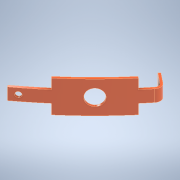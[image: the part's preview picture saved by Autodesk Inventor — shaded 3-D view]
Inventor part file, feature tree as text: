
AUTODESK INVENTOR PART (.ipt)
format: ipt  version: 2021 (Build 250183000, 183)  size: 205,824 bytes
history: native  units: in
note: dims shown in document units (in); Inventor stores cm internally (conversion verified against a paired STEP export)
features: other x5, sketch x4, extrude x1, plane x1
ambient origin geometry x8: Origin, YZ Plane, XZ Plane, XY Plane, X Axis, Y Axis, Z Axis, Center Point
bodies: Solid1 (feature_tree)
feature tree (11):
  extrude  "Extrusion1"  Depth=1.151in
  other  "Bend Part1"
  other  "Bend Part2"
  other  "Work Axis1"
  other  "Work Axis2"
  plane  "Work Plane1"
  sketch  "Sketch4"  dims[d6=0.0926in d8=0.11in d9=0.11in d10=0.0924in d11=0.218in d12=0.051in d13=0.055in d14=0.055in d15=0.051in d16=0.218in d17=0.1475in d18=0.148in d19=0.5755in d20=0.02in d21=0.0in d22=0.0394in d23=90.0deg d24=0.571in d25=0.2855in d26=3.9375in d27=360.0deg d28=0.148in d29=0.15in d30=0.75in d31=0.625in d32=0.7in]
  other  "Work Axis3"
  sketch  "Sketch1"  dims[d2=0.295in d3=1.151in]
  sketch  "Sketch2"  dims[d4=0.29in]
  sketch  "Sketch3"  dims[d5=0.29in]
